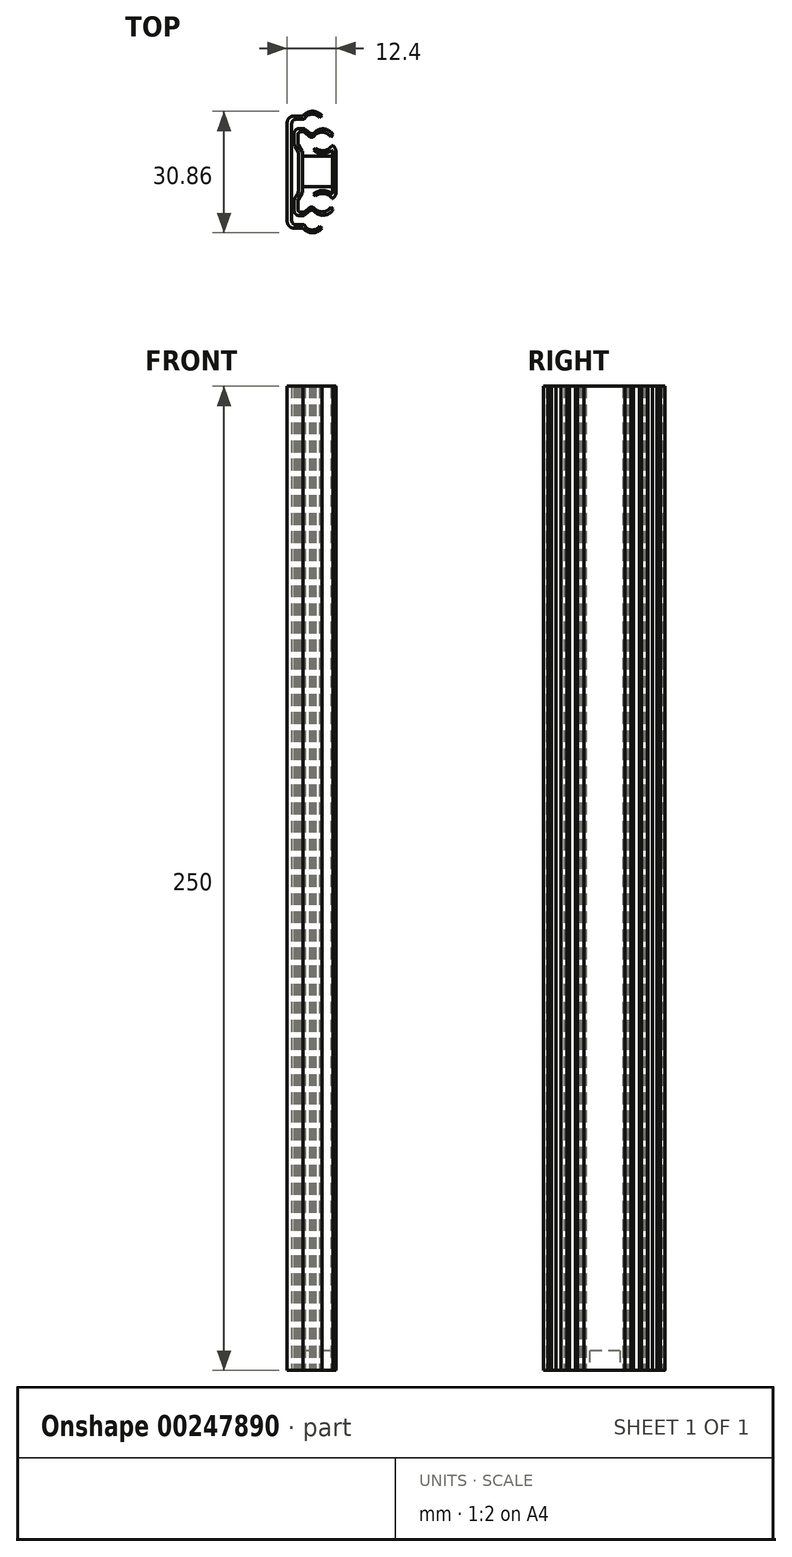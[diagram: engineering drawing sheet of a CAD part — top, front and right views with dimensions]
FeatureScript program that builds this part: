
annotation { "Feature Type Name" : "Feature", "Feature Type Description" : "" }
export const myFeature = defineFeature(function(context is Context, id is Id, definition is map)
    precondition{}
    {
        {
            var Q0;
            Q0=qCreatedBy(makeId("Top.planeOp"),FACE);
            var sketch = newSketch(context, id + "F0", { "sketchPlane" : qUnion([Q0])});
            skArc(sketch, "E0", {"start": v(-136.69, -0.39) * mm, "mid": v(-139.11, 0.73) * mm, "end": v(-141.51, -0.44) * mm});
            skArc(sketch, "E1", {"start": v(-137.3, -0.92) * mm, "mid": v(-139.36, 0.02) * mm, "end": v(-141.2, -1.29) * mm});
            skArc(sketch, "E2", {"start": v(-143.33, -1.29) * mm, "mid": v(-144.09, -1.65) * mm, "end": v(-144.36, -2.45) * mm});
            skArc(sketch, "E3", {"start": v(-143.76, -0.44) * mm, "mid": v(-145.04, -1) * mm, "end": v(-145.54, -2.3) * mm});
            skArc(sketch, "E4", {"start": v(-133.85, -5.23) * mm, "mid": v(-136.28, -3.73) * mm, "end": v(-138.85, -4.99) * mm});
            skArc(sketch, "E5", {"start": v(-134.42, -5.78) * mm, "mid": v(-136.7, -4.57) * mm, "end": v(-138.95, -5.83) * mm});
            skArc(sketch, "E6", {"start": v(-139.82, -5.65) * mm, "mid": v(-139.65, -5.77) * mm, "end": v(-139.45, -5.83) * mm});
            skArc(sketch, "E7", {"start": v(-141, -3.83) * mm, "mid": v(-141.22, -3.7) * mm, "end": v(-141.46, -3.64) * mm});
            skArc(sketch, "E8", {"start": v(-141.3, -6.65) * mm, "mid": v(-141.71, -6.76) * mm, "end": v(-141.89, -7.14) * mm});
            skArc(sketch, "E9", {"start": v(-139.75, -4.88) * mm, "mid": v(-139.54, -4.98) * mm, "end": v(-139.31, -4.99) * mm});
            skArc(sketch, "E10", {"start": v(-143.75, -7.34) * mm, "mid": v(-143.7, -7.78) * mm, "end": v(-143.5, -8.17) * mm});
            skArc(sketch, "E11", {"start": v(-142.81, -7.34) * mm, "mid": v(-142.8, -7.6) * mm, "end": v(-142.69, -7.85) * mm});
            skArc(sketch, "E12", {"start": v(-141.63, -9.73) * mm, "mid": v(-141.64, -9.56) * mm, "end": v(-141.7, -9.4) * mm});
            skArc(sketch, "E13", {"start": v(-142.7, -9.8) * mm, "mid": v(-142.73, -9.58) * mm, "end": v(-142.81, -9.37) * mm});
            skArc(sketch, "E14", {"start": v(-140.48, -7.53) * mm, "mid": v(-140.88, -7.73) * mm, "end": v(-140.94, -8.16) * mm});
            skArc(sketch, "E15", {"start": v(-140.96, -9.75) * mm, "mid": v(-140.98, -9.46) * mm, "end": v(-141.08, -9.2) * mm});
            skArc(sketch, "E16", {"start": v(-140.26, -9.82) * mm, "mid": v(-140.29, -9.47) * mm, "end": v(-140.44, -9.15) * mm});
            skArc(sketch, "E17", {"start": v(-138.31, -8.6) * mm, "mid": v(-136.06, -9.23) * mm, "end": v(-134.12, -7.94) * mm});
            skArc(sketch, "E18", {"start": v(-138.85, -9.1) * mm, "mid": v(-136.57, -10.01) * mm, "end": v(-134.28, -9.16) * mm});
            skArc(sketch, "E19", {"start": v(-133.14, -9.5) * mm, "mid": v(-133.4, -8.58) * mm, "end": v(-134.12, -7.94) * mm});
            skArc(sketch, "E20", {"start": v(-133.96, -9.75) * mm, "mid": v(-134.02, -9.4) * mm, "end": v(-134.28, -9.16) * mm});
            skLineSegment(sketch, "E21", {"start": v(-136.69, -0.39) * mm, "end": v(-137.3, -0.92) * mm});
            skLineSegment(sketch, "E22", {"start": v(-141.51, -0.44) * mm, "end": v(-143.76, -0.44) * mm});
            skLineSegment(sketch, "E23", {"start": v(-141.2, -1.29) * mm, "end": v(-143.33, -1.29) * mm});
            skLineSegment(sketch, "E24", {"start": v(-142.5, -3.64) * mm, "end": v(-141.46, -3.64) * mm});
            skLineSegment(sketch, "E25", {"start": v(-141, -3.83) * mm, "end": v(-139.75, -4.88) * mm});
            skLineSegment(sketch, "E26", {"start": v(-138.85, -4.99) * mm, "end": v(-139.31, -4.99) * mm});
            skLineSegment(sketch, "E27", {"start": v(-141, -4.64) * mm, "end": v(-139.82, -5.65) * mm});
            skLineSegment(sketch, "E28", {"start": v(-139.45, -5.83) * mm, "end": v(-138.95, -5.83) * mm});
            skLineSegment(sketch, "E29", {"start": v(-133.85, -5.23) * mm, "end": v(-134.42, -5.78) * mm});
            skLineSegment(sketch, "E30", {"start": v(-138.31, -8.6) * mm, "end": v(-138.85, -9.1) * mm});
            skLineSegment(sketch, "E31", {"start": v(-141.3, -6.65) * mm, "end": v(-134.23, -6.65) * mm});
            skLineSegment(sketch, "E32", {"start": v(-134.23, -6.65) * mm, "end": v(-134.23, -7.53) * mm});
            skLineSegment(sketch, "E33", {"start": v(-134.23, -7.53) * mm, "end": v(-140.48, -7.53) * mm});
            skLineSegment(sketch, "E34", {"start": v(-140.94, -8.16) * mm, "end": v(-140.44, -9.15) * mm});
            skArc(sketch, "E35", {"start": v(-141.89, -7.14) * mm, "mid": v(-141.87, -7.68) * mm, "end": v(-141.65, -8.18) * mm});
            skLineSegment(sketch, "E36", {"start": v(-141.65, -8.18) * mm, "end": v(-141.08, -9.2) * mm});
            skLineSegment(sketch, "E37", {"start": v(-141.7, -9.4) * mm, "end": v(-142.69, -7.85) * mm});
            skLineSegment(sketch, "E38", {"start": v(-142.81, -9.37) * mm, "end": v(-143.5, -8.17) * mm});
            skLineSegment(sketch, "E39", {"start": v(-143.75, -7.34) * mm, "end": v(-143.75, -5) * mm});
            skLineSegment(sketch, "E40", {"start": v(-142.81, -5.2) * mm, "end": v(-142.81, -7.34) * mm});
            skArc(sketch, "E41", {"start": v(-141, -4.64) * mm, "mid": v(-141.16, -4.54) * mm, "end": v(-141.35, -4.5) * mm});
            skArc(sketch, "E42", {"start": v(-142.08, -4.5) * mm, "mid": v(-142.6, -4.7) * mm, "end": v(-142.81, -5.2) * mm});
            skLineSegment(sketch, "E43", {"start": v(-142.08, -4.5) * mm, "end": v(-141.35, -4.5) * mm});
            skArc(sketch, "E44", {"start": v(-142.5, -3.64) * mm, "mid": v(-143.42, -4.04) * mm, "end": v(-143.75, -5) * mm});
            skLineSegment(sketch, "E45", {"start": v(-131.95, -14.7) * mm, "end": v(-148, -14.7) * mm, "construction": true});
            skArc(sketch, "E46.MirrorCS", {"start": v(-140.48, -21.87) * mm, "mid": v(-140.88, -21.67) * mm, "end": v(-140.94, -21.23) * mm});
            skArc(sketch, "E47.MirrorCS", {"start": v(-142.08, -24.9) * mm, "mid": v(-142.6, -24.7) * mm, "end": v(-142.81, -24.2) * mm});
            skArc(sketch, "E48.MirrorCS", {"start": v(-141.89, -22.26) * mm, "mid": v(-141.87, -21.72) * mm, "end": v(-141.65, -21.22) * mm});
            skArc(sketch, "E49.MirrorCS", {"start": v(-141, -24.76) * mm, "mid": v(-141.16, -24.86) * mm, "end": v(-141.35, -24.9) * mm});
            skArc(sketch, "E50.MirrorCS", {"start": v(-140.96, -19.65) * mm, "mid": v(-140.98, -19.93) * mm, "end": v(-141.08, -20.2) * mm});
            skArc(sketch, "E51.MirrorCS", {"start": v(-139.82, -23.75) * mm, "mid": v(-139.65, -23.63) * mm, "end": v(-139.45, -23.57) * mm});
            skArc(sketch, "E52.MirrorCS", {"start": v(-141, -25.56) * mm, "mid": v(-141.22, -25.7) * mm, "end": v(-141.46, -25.76) * mm});
            skArc(sketch, "E53.MirrorCS", {"start": v(-141.3, -22.75) * mm, "mid": v(-141.71, -22.64) * mm, "end": v(-141.89, -22.26) * mm});
            skArc(sketch, "E54.MirrorCS", {"start": v(-142.81, -22.05) * mm, "mid": v(-142.8, -21.79) * mm, "end": v(-142.69, -21.55) * mm});
            skArc(sketch, "E55.MirrorCS", {"start": v(-141.63, -19.67) * mm, "mid": v(-141.64, -19.84) * mm, "end": v(-141.7, -20) * mm});
            skLineSegment(sketch, "E56.MirrorCS", {"start": v(-141.7, -20) * mm, "end": v(-142.69, -21.55) * mm});
            skLineSegment(sketch, "E57.MirrorCS", {"start": v(-142.08, -24.9) * mm, "end": v(-141.35, -24.9) * mm});
            skLineSegment(sketch, "E58.MirrorCS", {"start": v(-142.5, -25.76) * mm, "end": v(-141.46, -25.76) * mm});
            skLineSegment(sketch, "E59.MirrorCS", {"start": v(-139.45, -23.57) * mm, "end": v(-138.95, -23.57) * mm});
            skLineSegment(sketch, "E60.MirrorCS", {"start": v(-141.65, -21.22) * mm, "end": v(-141.08, -20.2) * mm});
            skLineSegment(sketch, "E61.MirrorCS", {"start": v(-141, -25.56) * mm, "end": v(-139.75, -24.52) * mm});
            skLineSegment(sketch, "E62.MirrorCS", {"start": v(-138.85, -24.41) * mm, "end": v(-139.31, -24.41) * mm});
            skLineSegment(sketch, "E63.MirrorCS", {"start": v(-141.51, -28.96) * mm, "end": v(-143.76, -28.96) * mm});
            skArc(sketch, "E64.MirrorCS", {"start": v(-140.26, -19.57) * mm, "mid": v(-140.29, -19.93) * mm, "end": v(-140.44, -20.24) * mm});
            skLineSegment(sketch, "E65.MirrorCS", {"start": v(-142.81, -20.03) * mm, "end": v(-143.5, -21.23) * mm});
            skLineSegment(sketch, "E66.MirrorCS", {"start": v(-138.31, -20.79) * mm, "end": v(-138.85, -20.3) * mm});
            skLineSegment(sketch, "E67.MirrorCS", {"start": v(-136.69, -29) * mm, "end": v(-137.3, -28.47) * mm});
            skArc(sketch, "E68.MirrorCS", {"start": v(-143.75, -22.05) * mm, "mid": v(-143.7, -21.62) * mm, "end": v(-143.5, -21.23) * mm});
            skLineSegment(sketch, "E69.MirrorCS", {"start": v(-141.2, -28.11) * mm, "end": v(-143.33, -28.11) * mm});
            skArc(sketch, "E70.MirrorCS", {"start": v(-142.7, -19.6) * mm, "mid": v(-142.73, -19.82) * mm, "end": v(-142.81, -20.03) * mm});
            skLineSegment(sketch, "E71.MirrorCS", {"start": v(-142.81, -24.2) * mm, "end": v(-142.81, -22.05) * mm});
            skLineSegment(sketch, "E72.MirrorCS", {"start": v(-141, -24.76) * mm, "end": v(-139.82, -23.75) * mm});
            skArc(sketch, "E73.MirrorCS", {"start": v(-139.75, -24.52) * mm, "mid": v(-139.54, -24.42) * mm, "end": v(-139.31, -24.41) * mm});
            skLineSegment(sketch, "E74.MirrorCS", {"start": v(-133.85, -24.17) * mm, "end": v(-134.42, -23.61) * mm});
            skArc(sketch, "E75.MirrorCS", {"start": v(-133.96, -19.65) * mm, "mid": v(-134.02, -20) * mm, "end": v(-134.28, -20.24) * mm});
            skLineSegment(sketch, "E76.MirrorCS", {"start": v(-140.94, -21.23) * mm, "end": v(-140.44, -20.24) * mm});
            skLineSegment(sketch, "E77.MirrorCS", {"start": v(-134.23, -22.75) * mm, "end": v(-134.23, -21.87) * mm});
            skArc(sketch, "E78.MirrorCS", {"start": v(-133.14, -19.9) * mm, "mid": v(-133.4, -20.82) * mm, "end": v(-134.12, -21.46) * mm});
            skArc(sketch, "E79.MirrorCS", {"start": v(-143.33, -28.11) * mm, "mid": v(-144.09, -27.75) * mm, "end": v(-144.36, -26.95) * mm});
            skArc(sketch, "E80.MirrorCS", {"start": v(-138.85, -20.3) * mm, "mid": v(-136.57, -19.39) * mm, "end": v(-134.28, -20.24) * mm});
            skArc(sketch, "E81.MirrorCS", {"start": v(-136.69, -29) * mm, "mid": v(-139.11, -30.13) * mm, "end": v(-141.51, -28.96) * mm});
            skArc(sketch, "E82.MirrorCS", {"start": v(-137.3, -28.47) * mm, "mid": v(-139.36, -29.42) * mm, "end": v(-141.2, -28.11) * mm});
            skLineSegment(sketch, "E83.MirrorCS", {"start": v(-141.3, -22.75) * mm, "end": v(-134.23, -22.75) * mm});
            skArc(sketch, "E84.MirrorCS", {"start": v(-142.5, -25.76) * mm, "mid": v(-143.42, -25.35) * mm, "end": v(-143.75, -24.4) * mm});
            skLineSegment(sketch, "E85.MirrorCS", {"start": v(-134.23, -21.87) * mm, "end": v(-140.48, -21.87) * mm});
            skLineSegment(sketch, "E86.MirrorCS", {"start": v(-143.75, -22.05) * mm, "end": v(-143.75, -24.4) * mm});
            skArc(sketch, "E87.MirrorCS", {"start": v(-133.85, -24.17) * mm, "mid": v(-136.28, -25.67) * mm, "end": v(-138.85, -24.41) * mm});
            skArc(sketch, "E88.MirrorCS", {"start": v(-143.76, -28.96) * mm, "mid": v(-145.04, -28.4) * mm, "end": v(-145.54, -27.1) * mm});
            skArc(sketch, "E89.MirrorCS", {"start": v(-134.42, -23.61) * mm, "mid": v(-136.7, -24.82) * mm, "end": v(-138.95, -23.57) * mm});
            skArc(sketch, "E90.MirrorCS", {"start": v(-138.31, -20.79) * mm, "mid": v(-136.06, -20.17) * mm, "end": v(-134.12, -21.46) * mm});
            skLineSegment(sketch, "E91", {"start": v(-145.54, -2.3) * mm, "end": v(-145.54, -27.1) * mm});
            skLineSegment(sketch, "E92", {"start": v(-144.36, -26.95) * mm, "end": v(-144.36, -2.45) * mm});
            skLineSegment(sketch, "E93", {"start": v(-142.7, -9.8) * mm, "end": v(-142.7, -19.6) * mm});
            skLineSegment(sketch, "E94", {"start": v(-141.63, -9.73) * mm, "end": v(-141.63, -19.67) * mm});
            skLineSegment(sketch, "E95", {"start": v(-140.96, -19.65) * mm, "end": v(-140.96, -9.75) * mm});
            skLineSegment(sketch, "E96", {"start": v(-140.26, -9.82) * mm, "end": v(-140.26, -19.57) * mm});
            skLineSegment(sketch, "E97", {"start": v(-133.96, -9.75) * mm, "end": v(-133.96, -19.65) * mm});
            skLineSegment(sketch, "E98", {"start": v(-133.14, -19.9) * mm, "end": v(-133.14, -9.5) * mm});
            skSolve(sketch);
        }
        {
            var Q0;
            Q0=makeQuery(id+"F0.imprint","IMPRINT",FACE,{"disambiguationData":[TD([[makeQuery(id+"F0.imprint","IMPRINT",EDGE,{"derivedFrom":sQuery(id+"F0.wireOp",EDGE,"E0")}),1.0]])]});
            extrude(context, id + "F1", {"entities" : qUnion([Q0]), "depth" : 250 * mm});
        }
        {
            var Q0;
            Q0=makeQuery(id+"F0.imprint","IMPRINT",FACE,{"disambiguationData":[TD([[makeQuery(id+"F0.imprint","IMPRINT",EDGE,{"derivedFrom":sQuery(id+"F0.wireOp",EDGE,"E4")}),1.0]])]});
            var Q1;
            Q1=makeQuery(id+"F0.imprint","IMPRINT",FACE,{"disambiguationData":[TD([[makeQuery(id+"F0.imprint","IMPRINT",EDGE,{"derivedFrom":sQuery(id+"F0.wireOp",EDGE,"E17")}),-1.0]])]});
            extrude(context, id + "F2", {"entities" : qUnion([Q0, Q1]), "depth" : 250 * mm});
        }
        {
            var Q0;
            Q0=qCreatedBy(makeId("Top.planeOp"),FACE);
            var sketch = newSketch(context, id + "F3", { "sketchPlane" : qUnion([Q0])});
            skLineSegment(sketch, "E99.bottom", {"start": v(-133.47, -18.42) * mm, "end": v(-142.12, -18.42) * mm});
            skLineSegment(sketch, "E99.top", {"start": v(-133.47, -10.7) * mm, "end": v(-142.12, -10.7) * mm});
            skLineSegment(sketch, "E99.left", {"start": v(-133.47, -18.42) * mm, "end": v(-133.47, -10.7) * mm});
            skLineSegment(sketch, "E99.right", {"start": v(-142.12, -18.42) * mm, "end": v(-142.12, -10.7) * mm});
            skSolve(sketch);
        }
        {
            var Q0;
            Q0=makeQuery(id+"F3.imprint","IMPRINT",FACE,{"disambiguationData":[TD([[makeQuery(id+"F3.imprint","IMPRINT",EDGE,{"derivedFrom":sQuery(id+"F3.wireOp",EDGE,"E99.bottom")}),-1.0]])]});
            extrude(context, id + "F4", {"entities" : qUnion([Q0]), "operationType" : NewBodyOperationType.ADD, "depth" : 5 * mm});
        }
    });
